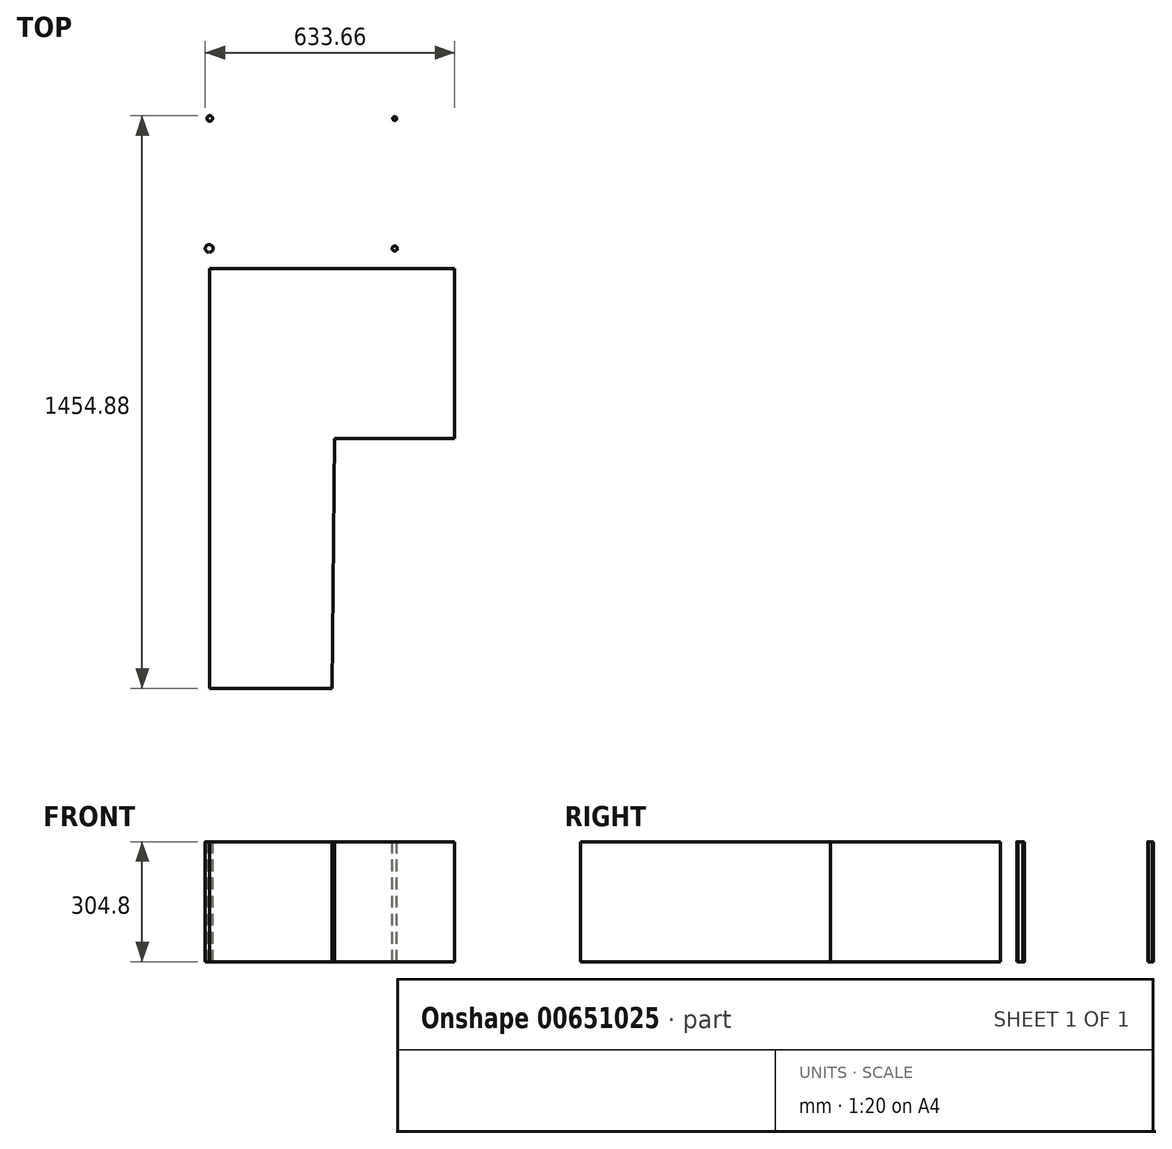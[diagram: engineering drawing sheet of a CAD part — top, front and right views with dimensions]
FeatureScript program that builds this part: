
annotation { "Feature Type Name" : "Feature", "Feature Type Description" : "" }
export const myFeature = defineFeature(function(context is Context, id is Id, definition is map)
    precondition{}
    {
        {
            var Q0;
            Q0=qCreatedBy(makeId("Top.planeOp"),FACE);
            var sketch = newSketch(context, id + "F0", { "sketchPlane" : qUnion([Q0])});
            skLineSegment(sketch, "E0", {"start": v(-310.5, 301.61) * mm, "end": v(311.8, 301.61) * mm});
            skLineSegment(sketch, "E1", {"start": v(311.8, 301.61) * mm, "end": v(311.8, -130.19) * mm});
            skLineSegment(sketch, "E2", {"start": v(311.8, -130.19) * mm, "end": v(7, -130.19) * mm});
            skLineSegment(sketch, "E3", {"start": v(-310.5, 301.61) * mm, "end": v(-310.5, -765.19) * mm});
            skLineSegment(sketch, "E4", {"start": v(7, -130.19) * mm, "end": v(0, -765.15) * mm});
            skLineSegment(sketch, "E5", {"start": v(-310.5, -765.19) * mm, "end": v(0, -765.15) * mm});
            skSolve(sketch);
        }
        {
            var Q0;
            Q0=makeQuery(id+"F0.imprint","IMPRINT",FACE,{"disambiguationData":[TD([[makeQuery(id+"F0.imprint","IMPRINT",EDGE,{"derivedFrom":sQuery(id+"F0.wireOp",EDGE,"E0")}),-1.0]])]});
            extrude(context, id + "F1", {"entities" : qUnion([Q0]), "depth" : 304.8 * mm, "offsetDistance" : 25.4 * mm});
        }
        {
            var Q0;
            Q0=makeQuery(id+"F1.opExtrude","CAP_FACE",FACE,{"disambiguationData":[OSD([sQuery(id+"F0.wireOp",EDGE,"E0"),sQuery(id+"F0.wireOp",EDGE,"E1"),sQuery(id+"F0.wireOp",EDGE,"E2"),sQuery(id+"F0.wireOp",EDGE,"E3"),sQuery(id+"F0.wireOp",EDGE,"E4"),sQuery(id+"F0.wireOp",EDGE,"E5")])],"isStart":false});
            var sketch = newSketch(context, id + "F2", { "sketchPlane" : qUnion([Q0])});
            skCircle(sketch, "E6", {"center": v(-312.05, 352.41) * mm, "radius": 9.81 * mm});
            skCircle(sketch, "E7", {"center": v(159.4, 352.41) * mm, "radius": 6.38 * mm});
            skCircle(sketch, "E8", {"center": v(159.4, 682.61) * mm, "radius": 4.98 * mm});
            skCircle(sketch, "E9", {"center": v(-310.5, 682.61) * mm, "radius": 7.08 * mm});
            skSolve(sketch);
        }
        {
            var Q0;
            Q0 = qSketchRegion(id + "F2", true);
            extrude(context, id + "F3", {"entities" : qUnion([Q0]), "depth" : -304.8 * mm, "offsetDistance" : 25.4 * mm});
        }
    });
